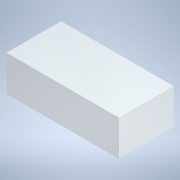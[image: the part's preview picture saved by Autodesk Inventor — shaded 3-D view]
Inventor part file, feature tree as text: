
AUTODESK INVENTOR PART (.ipt)
format: ipt  version: 2020 (Build 240168000, 168)  size: 95,744 bytes
history: native  units: mm
features: other x1, extrude x1, sketch x1
ambient origin geometry x8: Origin, YZ Plane, XZ Plane, XY Plane, X Axis, Y Axis, Z Axis, Center Point
bodies: Body1 (feature_tree)
feature tree (3):
  other  "Bryła1"
  extrude  "Wyciągnięcie proste1"  Depth=36.0mm
  sketch  "Szkic1"
